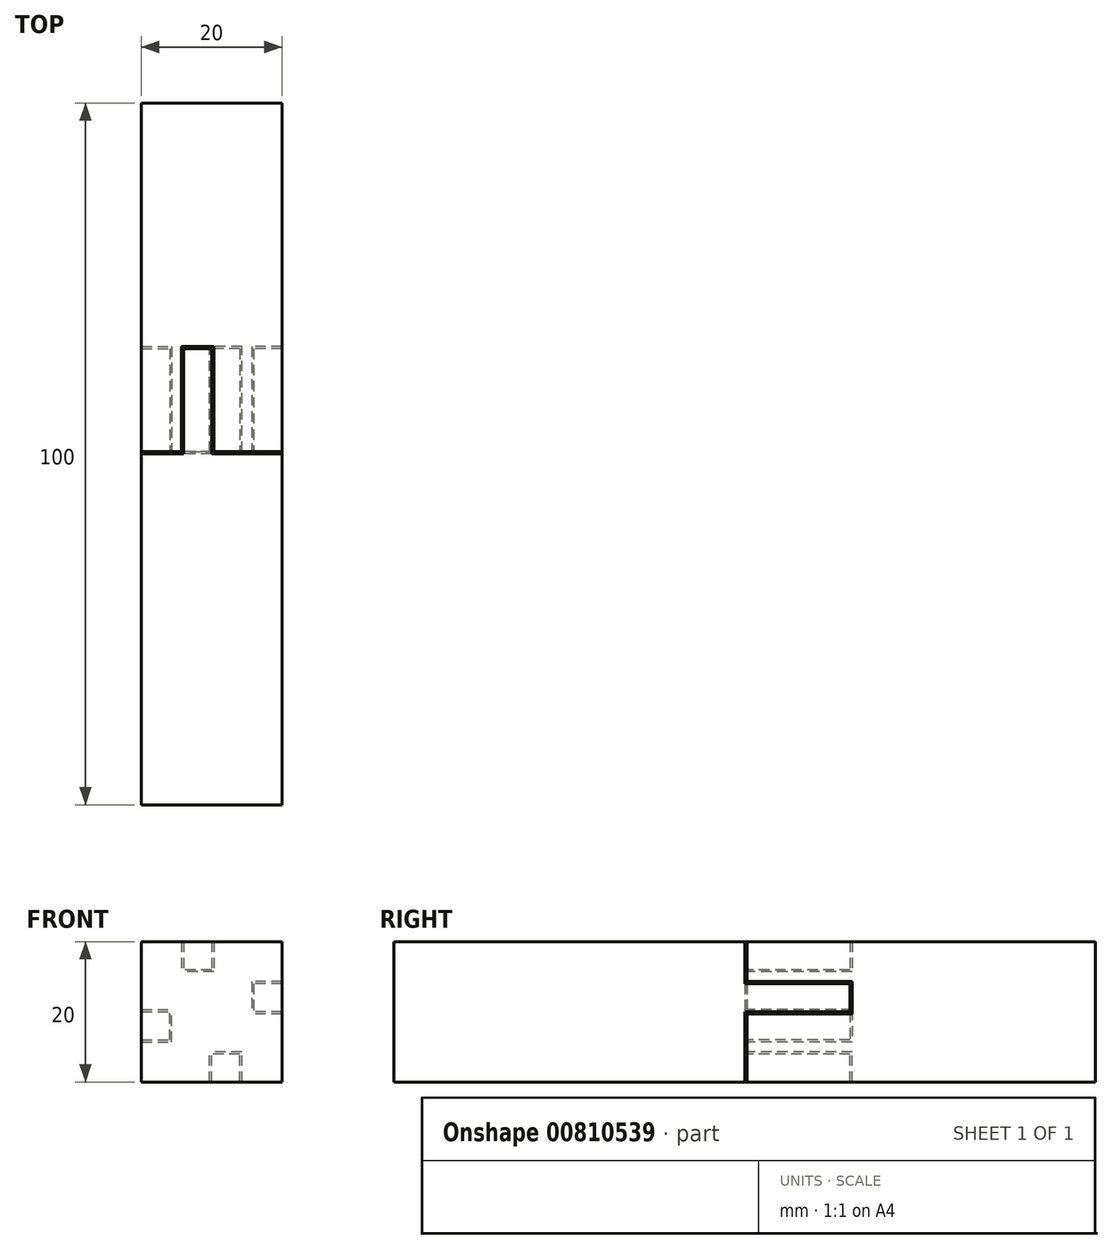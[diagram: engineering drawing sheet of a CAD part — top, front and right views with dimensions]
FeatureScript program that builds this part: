
annotation { "Feature Type Name" : "Feature", "Feature Type Description" : "" }
export const myFeature = defineFeature(function(context is Context, id is Id, definition is map)
    precondition{}
    {
        {
            var Q0;
            Q0=qCreatedBy(makeId("Front.planeOp"),FACE);
            var sketch = newSketch(context, id + "F0", { "sketchPlane" : qUnion([Q0])});
            skLineSegment(sketch, "E0.bottom", {"start": v(10, 10) * mm, "end": v(-10, 10) * mm});
            skLineSegment(sketch, "E0.top", {"start": v(10, -10) * mm, "end": v(-10, -10) * mm});
            skLineSegment(sketch, "E0.left", {"start": v(10, 10) * mm, "end": v(10, -10) * mm});
            skLineSegment(sketch, "E0.right", {"start": v(-10, 10) * mm, "end": v(-10, -10) * mm});
            skPoint(sketch, "E0.middle", {"position": v(0, 0) * mm});
            skSolve(sketch);
        }
        {
            var Q0;
            Q0=makeQuery(id+"F0.imprint","IMPRINT",FACE,{"disambiguationData":[TD([[makeQuery(id+"F0.imprint","IMPRINT",EDGE,{"derivedFrom":sQuery(id+"F0.wireOp",EDGE,"E0.bottom")}),1.0]])]});
            extrude(context, id + "F1", {"entities" : qUnion([Q0]), "depth" : 50 * mm, "offsetDistance" : 25 * mm});
        }
        {
            var Q0;
            Q0=makeQuery(id+"F1.opExtrude","CAP_FACE",FACE,{"disambiguationData":[OSD([sQuery(id+"F0.wireOp",EDGE,"E0.bottom"),sQuery(id+"F0.wireOp",EDGE,"E0.top"),sQuery(id+"F0.wireOp",EDGE,"E0.left"),sQuery(id+"F0.wireOp",EDGE,"E0.right")])],"isStart":true});
            var sketch = newSketch(context, id + "F2", { "sketchPlane" : qUnion([Q0])});
            skLineSegment(sketch, "E1.bottom", {"start": v(0, 10) * mm, "end": v(4, 10) * mm});
            skLineSegment(sketch, "E1.top", {"start": v(0, 6) * mm, "end": v(4, 6) * mm});
            skLineSegment(sketch, "E1.left", {"start": v(0, 10) * mm, "end": v(0, 6) * mm});
            skLineSegment(sketch, "E1.right", {"start": v(4, 10) * mm, "end": v(4, 6) * mm});
            skLineSegment(sketch, "E2.bottom", {"start": v(-4, -10) * mm, "end": v(0, -10) * mm});
            skLineSegment(sketch, "E2.top", {"start": v(-4, -6) * mm, "end": v(0, -6) * mm});
            skLineSegment(sketch, "E2.left", {"start": v(-4, -10) * mm, "end": v(-4, -6) * mm});
            skLineSegment(sketch, "E2.right", {"start": v(0, -10) * mm, "end": v(0, -6) * mm});
            skLineSegment(sketch, "E3.bottom", {"start": v(10, -4) * mm, "end": v(6, -4) * mm});
            skLineSegment(sketch, "E3.top", {"start": v(10, 0) * mm, "end": v(6, 0) * mm});
            skLineSegment(sketch, "E3.left", {"start": v(10, -4) * mm, "end": v(10, 0) * mm});
            skLineSegment(sketch, "E3.right", {"start": v(6, -4) * mm, "end": v(6, 0) * mm});
            skLineSegment(sketch, "E4.bottom", {"start": v(-10, 4) * mm, "end": v(-6, 4) * mm});
            skLineSegment(sketch, "E4.top", {"start": v(-10, 0) * mm, "end": v(-6, 0) * mm});
            skLineSegment(sketch, "E4.left", {"start": v(-10, 4) * mm, "end": v(-10, 0) * mm});
            skLineSegment(sketch, "E4.right", {"start": v(-6, 4) * mm, "end": v(-6, 0) * mm});
            skSolve(sketch);
        }
        {
            var Q0;
            Q0=qSketchRegion(id+"F2",true);
            extrude(context, id + "F3", {"entities" : qUnion([Q0]), "operationType" : NewBodyOperationType.ADD, "depth" : 15 * mm, "offsetDistance" : 25 * mm});
        }
        {
            var Q0;
            Q0=qCreatedBy(makeId("Front.planeOp"),FACE);
            var sketch = newSketch(context, id + "F4", { "sketchPlane" : qUnion([Q0])});
            skPoint(sketch, "E5.middle", {"position": v(0, 0) * mm});
            skLineSegment(sketch, "E6.0", {"start": v(10, 10) * mm, "end": v(0, 10) * mm, "construction": true});
            skLineSegment(sketch, "E7.0", {"start": v(-10, -4) * mm, "end": v(-10, -10) * mm, "construction": true});
            skLineSegment(sketch, "E8.bottom", {"start": v(10, 10) * mm, "end": v(-10, 10) * mm});
            skLineSegment(sketch, "E8.top", {"start": v(10, -10) * mm, "end": v(-10, -10) * mm});
            skLineSegment(sketch, "E8.left", {"start": v(10, 10) * mm, "end": v(10, -10) * mm});
            skLineSegment(sketch, "E8.right", {"start": v(-10, 10) * mm, "end": v(-10, -10) * mm});
            skSolve(sketch);
        }
        {
            var Q0;
            Q0=qSketchRegion(id+"F4",true);
            extrude(context, id + "F5", {"entities" : qUnion([Q0]), "oppositeDirection" : true, "depth" : 50 * mm, "offsetDistance" : 25 * mm});
        }
        {
            var Q0;
            Q0=makeQuery(id+"F1.opExtrude","SWEPT_BODY",BODY,{"disambiguationData":[OSD([sQuery(id+"F0.wireOp",EDGE,"E0.bottom"),sQuery(id+"F0.wireOp",EDGE,"E0.top"),sQuery(id+"F0.wireOp",EDGE,"E0.left"),sQuery(id+"F0.wireOp",EDGE,"E0.right")])]});
            var Q1;
            Q1=makeQuery(id+"F5.opExtrude","SWEPT_BODY",BODY,{"disambiguationData":[OSD([sQuery(id+"F4.wireOp",EDGE,"E8.bottom"),sQuery(id+"F4.wireOp",EDGE,"E8.top"),sQuery(id+"F4.wireOp",EDGE,"E8.left"),sQuery(id+"F4.wireOp",EDGE,"E8.right")])]});
            booleanBodies(context, id + "F6", {"operationType" : BooleanOperationType.SUBTRACTION, "tools" : qUnion([Q0]), "targets" : qUnion([Q1]), "offset" : true, "offsetAll" : true, "offsetDistance" : 0.3 * mm, "keepTools" : true});
        }
    });
